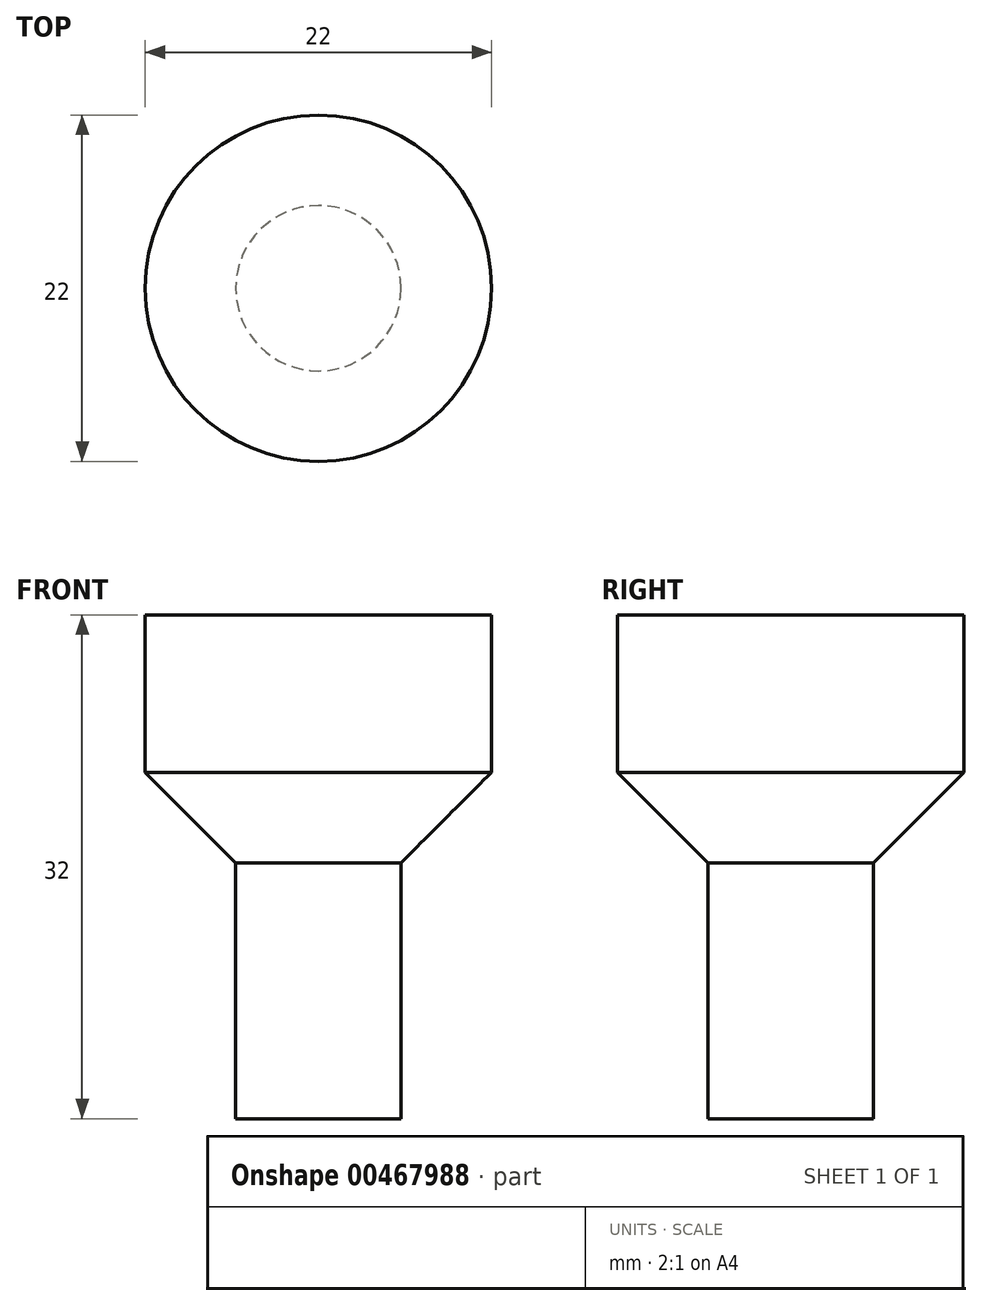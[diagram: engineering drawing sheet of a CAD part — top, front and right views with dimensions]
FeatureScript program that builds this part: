
annotation { "Feature Type Name" : "Feature", "Feature Type Description" : "" }
export const myFeature = defineFeature(function(context is Context, id is Id, definition is map)
    precondition{}
    {
        {
            assignVariable(context, id + "F0", {"name" : "ShaftDepth", "anyValue" : 22 * mm});
        }
        {
            assignVariable(context, id + "F1", {"name" : "JointHeight", "anyValue" : 10 * mm});
        }
        {
            var Q0;
            Q0=qCreatedBy(makeId("Top.planeOp"),FACE);
            var sketch = newSketch(context, id + "F2", { "sketchPlane" : qUnion([Q0])});
            skCircle(sketch, "E0", {"center": v(0, 0) * mm, "radius": 5.25 * mm});
            skSolve(sketch);
        }
        {
            var Q0;
            Q0 = qSketchRegion(id + "F2", true);
            extrude(context, id + "F3", {"entities" : qUnion([Q0]), "depth" : getVariable(context, 'ShaftDepth')});
        }
        {
            var Q0;
            Q0=qCreatedBy(makeId("Top.planeOp"),FACE);
            var sketch = newSketch(context, id + "F4", { "sketchPlane" : qUnion([Q0])});
            skCircle(sketch, "E1", {"center": v(0, 0) * mm, "radius": 11 * mm});
            skSolve(sketch);
        }
        {
            var Q0;
            Q0 = qSketchRegion(id + "F4", true);
            extrude(context, id + "F5", {"entities" : qUnion([Q0]), "operationType" : NewBodyOperationType.ADD, "depth" : getVariable(context, 'ShaftDepth') + getVariable(context, 'JointHeight'), "hasSecondDirection" : true, "secondDirectionOppositeDirection" : false, "secondDirectionDepth" : getVariable(context, 'ShaftDepth')});
        }
        {
            var Q0;
            Q0=qCreatedBy(makeId("Front.planeOp"),FACE);
            var sketch = newSketch(context, id + "F6", { "sketchPlane" : qUnion([Q0])});
            skLineSegment(sketch, "E2", {"start": v(0, 22) * mm, "end": v(-11, 22) * mm});
            skLineSegment(sketch, "E3", {"start": v(-11, 22) * mm, "end": v(0, 11) * mm});
            skLineSegment(sketch, "E4", {"start": v(0, 11) * mm, "end": v(0, 22) * mm});
            skSolve(sketch);
        }
        {
            var Q0;
            Q0 = qSketchRegion(id + "F6", true);
            var Q1;
            Q1=sQuery(id+"F6.wireOp",EDGE,"E4");
            revolve(context, id + "F7", {"operationType" : NewBodyOperationType.ADD, "entities" : qUnion([Q0]), "axis" : qUnion([Q1]), "revolveType" : RevolveType.FULL});
        }
    });
